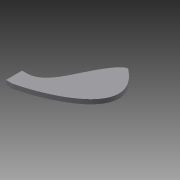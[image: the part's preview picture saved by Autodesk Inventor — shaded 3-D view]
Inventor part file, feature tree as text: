
AUTODESK INVENTOR PART (.ipt)
format: ipt  version: 2015 (Build 190159000, 159)  size: 78,848 bytes
history: native  units: mm
features: extrude x1, sketch x1
ambient origin geometry x8: Origin, YZ Plane, XZ Plane, XY Plane, X Axis, Y Axis, Z Axis, Center Point
bodies: Solid1 (feature_tree)
feature tree (2):
  extrude  "Extrusion1"  Depth=8.0mm
  sketch  "Sketch1"  dims[d4=5.5mm d5=0.0mm d6=8.0mm]
